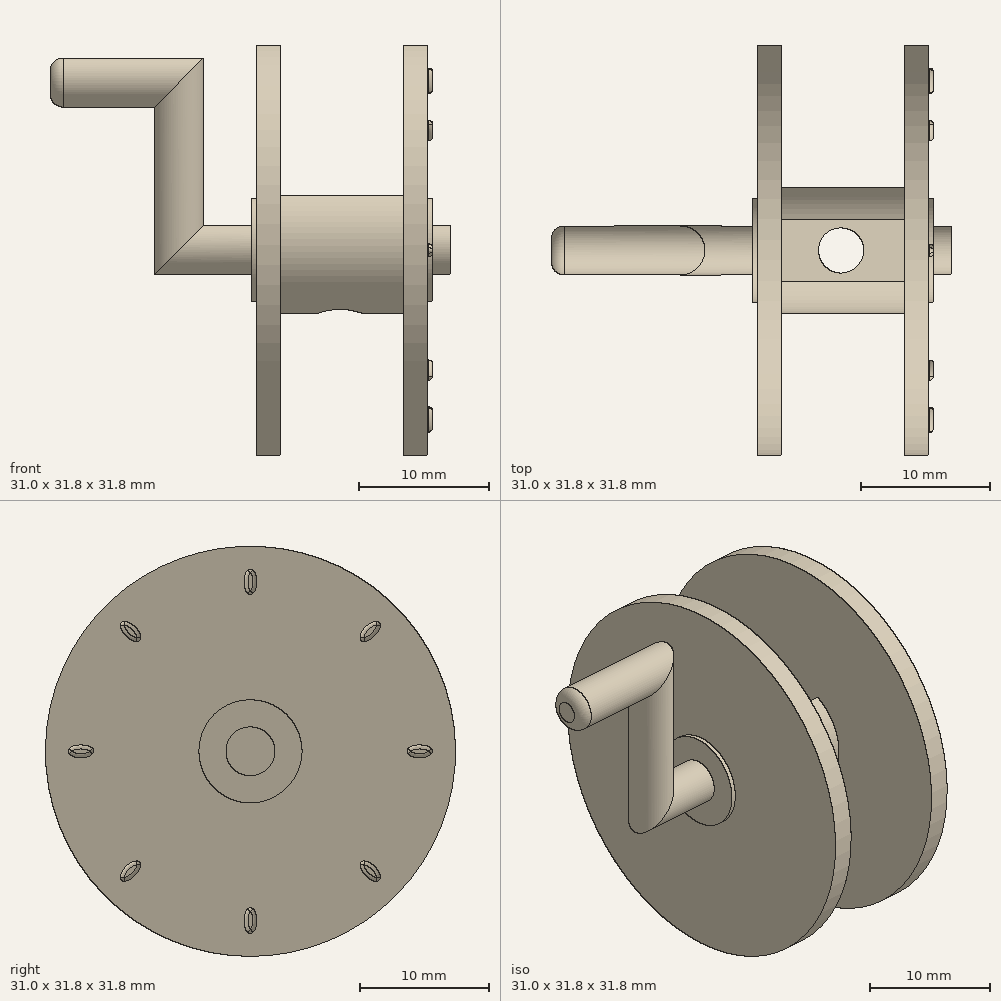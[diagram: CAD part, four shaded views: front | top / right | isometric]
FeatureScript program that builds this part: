
annotation { "Feature Type Name" : "Feature", "Feature Type Description" : "" }
export const myFeature = defineFeature(function(context is Context, id is Id, definition is map)
    precondition{}
    {
        {
            var Q0;
            Q0=qCreatedBy(makeId("Right.planeOp"),FACE);
            var sketch = newSketch(context, id + "F0", { "sketchPlane" : qUnion([Q0])});
            skCircle(sketch, "E0", {"center": v(0, 0) * mm, "radius": 15.9 * mm});
            skSolve(sketch);
        }
        {
            var Q0;
            Q0=makeQuery(id+"F0.imprint","IMPRINT",FACE,{"disambiguationData":[TD([[makeQuery(id+"F0.imprint","IMPRINT",EDGE,{"derivedFrom":sQuery(id+"F0.wireOp",EDGE,"E0")}),1.0]])]});
            var Q1;
            Q1=sQuery(id+"F0.wireOp",EDGE,"E0");
            extrude(context, id + "F1", {"entities" : qUnion([Q0]), "surfaceEntities" : qUnion([Q1]), "depth" : 1.85 * mm, "offsetDistance" : 25 * mm});
        }
        {
            var Q0;
            Q0=makeQuery(id+"F1.opExtrude","CAP_FACE",FACE,{"disambiguationData":[OSD([sQuery(id+"F0.wireOp",EDGE,"E0")])],"isStart":false});
            var sketch = newSketch(context, id + "F2", { "sketchPlane" : qUnion([Q0])});
            skCircle(sketch, "E1", {"center": v(0, 0) * mm, "radius": 4.9 * mm});
            skSolve(sketch);
        }
        {
            var Q0;
            Q0 = qSketchRegion(id + "F2", true);
            extrude(context, id + "F3", {"entities" : qUnion([Q0]), "operationType" : NewBodyOperationType.ADD, "depth" : 9.55 * mm, "offsetDistance" : 25 * mm});
        }
        {
            var Q0;
            Q0=makeQuery(id+"F3.opExtrude","CAP_FACE",FACE,{"disambiguationData":[OSD([sQuery(id+"F2.wireOp",EDGE,"E1")])],"isStart":false});
            var sketch = newSketch(context, id + "F4", { "sketchPlane" : qUnion([Q0])});
            skCircle(sketch, "E2", {"center": v(0, 0) * mm, "radius": 15.9 * mm});
            skSolve(sketch);
        }
        {
            var Q0;
            Q0 = qSketchRegion(id + "F4", true);
            extrude(context, id + "F5", {"entities" : qUnion([Q0]), "operationType" : NewBodyOperationType.ADD, "depth" : 1.85 * mm, "offsetDistance" : 25 * mm});
        }
        {
            var Q0;
            Q0=makeQuery(id+"F5.opExtrude","CAP_FACE",FACE,{"disambiguationData":[OSD([sQuery(id+"F4.wireOp",EDGE,"E2")])],"isStart":false});
            var sketch = newSketch(context, id + "F6", { "sketchPlane" : qUnion([Q0])});
            skCircle(sketch, "E3", {"center": v(0, 0) * mm, "radius": 1.9 * mm});
            skSolve(sketch);
        }
        {
            var Q0;
            Q0 = qSketchRegion(id + "F6", true);
            extrude(context, id + "F7", {"entities" : qUnion([Q0]), "operationType" : NewBodyOperationType.ADD, "depth" : 1.78 * mm, "offsetDistance" : 25 * mm});
        }
        {
            var Q0;
            Q0=makeQuery(id+"F1.opExtrude","CAP_FACE",FACE,{"disambiguationData":[OSD([sQuery(id+"F0.wireOp",EDGE,"E0")])],"isStart":true});
            var sketch = newSketch(context, id + "F8", { "sketchPlane" : qUnion([Q0])});
            skCircle(sketch, "E4", {"center": v(0, 0) * mm, "radius": 1.9 * mm});
            skSolve(sketch);
        }
        {
            var Q0;
            Q0=qCreatedBy(makeId("Front.planeOp"),FACE);
            var sketch = newSketch(context, id + "F9", { "sketchPlane" : qUnion([Q0])});
            skLineSegment(sketch, "E5", {"start": v(0, 0) * mm, "end": v(-6, 0) * mm});
            skLineSegment(sketch, "E6", {"start": v(-6, 0) * mm, "end": v(-6, 13) * mm});
            skLineSegment(sketch, "E7", {"start": v(-6, 13) * mm, "end": v(-16, 13) * mm});
            skSolve(sketch);
        }
        {
            var Q0;
            Q0=makeQuery(id+"F8.imprint","IMPRINT",FACE,{"disambiguationData":[TD([[makeQuery(id+"F8.imprint","IMPRINT",EDGE,{"derivedFrom":sQuery(id+"F8.wireOp",EDGE,"E4")}),1.0]])]});
            var Q1;
            Q1=sQuery(id+"F9.wireOp",EDGE,"E5");
            var Q2;
            Q2=sQuery(id+"F9.wireOp",EDGE,"E6");
            var Q3;
            Q3=sQuery(id+"F9.wireOp",EDGE,"E7");
            sweep(context, id + "F10", {"operationType" : NewBodyOperationType.ADD, "profiles" : qUnion([Q0]), "path" : qUnion([Q1, Q2, Q3])});
        }
        {
            var Q0;
            Q0=makeQuery(id+"F10.opSweep","CAP_EDGE",EDGE,{"disambiguationData":[OSD([sQuery(id+"F8.wireOp",EDGE,"E4"),sQuery(id+"F9.wireOp",VERTEX,"E7.end")])],"isStart":false});
            fillet(context, id + "F11", {"entities" : qUnion([Q0]), "radius" : 1 * mm, "tangentPropagation" : true, "allowEdgeOverflow" : false});
        }
        {
            var Q0;
            Q0=makeQuery(id+"F5.opExtrude","CAP_FACE",FACE,{"disambiguationData":[OSD([sQuery(id+"F4.wireOp",EDGE,"E2")])],"isStart":false});
            var sketch = newSketch(context, id + "F12", { "sketchPlane" : qUnion([Q0])});
            skEllipse(sketch, "E8", {"center": v(13.13, 0) * mm, "majorRadius": 1 * mm, "minorRadius": 0.5 * mm, "majorAxis": v(-1, 0)});
            skSolve(sketch);
        }
        {
            var Q0;
            Q0=makeQuery(id+"F12.imprint","IMPRINT",FACE,{"disambiguationData":[TD([[makeQuery(id+"F12.imprint","IMPRINT",EDGE,{"derivedFrom":sQuery(id+"F12.wireOp",EDGE,"E8")}),1.0]])]});
            extrude(context, id + "F13", {"entities" : qUnion([Q0]), "depth" : 0.4 * mm, "offsetDistance" : 25 * mm});
        }
        {
            var Q0;
            Q0=makeQuery(id+"F13.opExtrude","CAP_FACE",FACE,{"disambiguationData":[OSD([sQuery(id+"F12.wireOp",EDGE,"E8")])],"isStart":false});
            fillet(context, id + "F14", {"entities" : qUnion([Q0]), "radius" : 0.31 * mm, "allowEdgeOverflow" : false});
        }
        {
            var Q0;
            Q0=makeQuery(id+"F13.opExtrude","SWEPT_BODY",BODY,{"disambiguationData":[OSD([sQuery(id+"F12.wireOp",EDGE,"E8")])]});
            var Q1;
            Q1=makeQuery(id+"F7.opExtrude","CAP_EDGE",EDGE,{"disambiguationData":[OSD([sQuery(id+"F6.wireOp",EDGE,"E3")])],"isStart":false});
            circularPattern(context, id + "F15", {"entities" : qUnion([Q0]), "axis" : qUnion([Q1]), "angle" : 360 * degree, "instanceCount" : 8, "equalSpace" : true});
        }
        {
            var Q0;
            Q0=makeQuery(id+"F5.opExtrude","CAP_FACE",FACE,{"disambiguationData":[OSD([sQuery(id+"F4.wireOp",EDGE,"E2")])],"isStart":false});
            var sketch = newSketch(context, id + "F16", { "sketchPlane" : qUnion([Q0])});
            skCircle(sketch, "E9", {"center": v(0, 0) * mm, "radius": 4 * mm});
            skSolve(sketch);
        }
        {
            var Q0;
            Q0 = qSketchRegion(id + "F16", true);
            extrude(context, id + "F17", {"entities" : qUnion([Q0]), "operationType" : NewBodyOperationType.ADD, "depth" : 0.4 * mm, "offsetDistance" : 25 * mm});
        }
        {
            var Q0;
            Q0=makeQuery(id+"F1.opExtrude","CAP_FACE",FACE,{"disambiguationData":[OSD([sQuery(id+"F0.wireOp",EDGE,"E0")])],"isStart":true});
            var sketch = newSketch(context, id + "F18", { "sketchPlane" : qUnion([Q0])});
            skCircle(sketch, "E10", {"center": v(0, 0) * mm, "radius": 4 * mm});
            skSolve(sketch);
        }
        {
            var Q0;
            Q0 = qSketchRegion(id + "F18", true);
            extrude(context, id + "F19", {"entities" : qUnion([Q0]), "operationType" : NewBodyOperationType.ADD, "depth" : 0.4 * mm, "offsetDistance" : 25 * mm});
        }
        {
            var Q0;
            Q0=qCreatedBy(makeId("Top.planeOp"),FACE);
            cPlane(context, id + "F20", {"entities" : qUnion([Q0]), "cplaneType" : CPlaneType.OFFSET, "offset" : 4.9 * mm, "width" : 150 * mm, "height" : 150 * mm});
        }
        {
            var Q0;
            Q0=qCreatedBy(id+"F20.planeOp",FACE);
            var sketch = newSketch(context, id + "F21", { "sketchPlane" : qUnion([Q0])});
            skCircle(sketch, "E11", {"center": v(6.47, 0) * mm, "radius": 1.75 * mm});
            skSolve(sketch);
        }
        {
            var Q0;
            Q0 = qSketchRegion(id + "F21", true);
            extrude(context, id + "F22", {"entities" : qUnion([Q0]), "operationType" : NewBodyOperationType.REMOVE, "oppositeDirection" : true, "depth" : 10 * mm, "offsetDistance" : 25 * mm});
        }
        {
            var Q0;
            Q0=qCreatedBy(id+"F20.planeOp",FACE);
            var sketch = newSketch(context, id + "F23", { "sketchPlane" : qUnion([Q0])});
            skLineSegment(sketch, "E12.bottom", {"start": v(11.4, -2.4) * mm, "end": v(1.85, -2.4) * mm});
            skLineSegment(sketch, "E12.top", {"start": v(11.4, 2.4) * mm, "end": v(1.85, 2.4) * mm});
            skLineSegment(sketch, "E12.left", {"start": v(11.4, -2.4) * mm, "end": v(11.4, 2.4) * mm});
            skLineSegment(sketch, "E12.right", {"start": v(1.85, -2.4) * mm, "end": v(1.85, 2.4) * mm});
            skSolve(sketch);
        }
        {
            var Q0;
            Q0 = qSketchRegion(id + "F23", true);
            extrude(context, id + "F24", {"entities" : qUnion([Q0]), "operationType" : NewBodyOperationType.REMOVE, "oppositeDirection" : true, "depth" : 4 * mm, "offsetDistance" : 25 * mm});
        }
    });
